# Revit family: QF_ALPENINOX_713294_AC6R4RL
name_source: partatom
category: Attrezzature speciali
revit_build: Autodesk Revit 2018 (Build: 20181011_1500(x64)
units: mm (PartAtom-declared; Revit-internal decimal feet)

## family parameters
Basato su piano di lavoro = No
Condiviso = No
Punto di calcolo locali = No
Quota connettore circolare = Usa diametro
Sempre verticale = Sì
Taglio con vuoti quando caricato = No
Tipo di parte = Normale

## types (1)
- Standard
    Accessory = Sì
    Cold Water Size = 0 mm
    Compressed Air Pressure = 0.0 Pa
    Compressed Air Size = 0 mm
    Compressed Air Volume = 0.0 L/s
    Condensate Return Size = 0 mm
    Cycle = 50 Hz
    Depth Actual = 700 mm  [stored 2.29659 ft]
    Descrizione = REFR.COUNTER 590L 2xDOOR 4x1/2DRW NOTOP REM CU_LFT A304
    Direct Waste Size = 0 mm
    Gas Input Pressure = 0
    Gas KW = 0
    Gas Size = 0 mm
    HP = 0 HP
    Height Actual = 800 mm  [stored 2.62467 ft]
    Hot Water Size = 0 mm
    Item Number = 713294
    Length Actual = 2012 mm  [stored 6.60105 ft]
    Modello = AC6R4RL
    Phase = 1
    Produttore = Alpeninox
    Refrigerant Compressor Remote = Sì
    Refrigeration Liquid Line Size = 8 mm  [stored 0.0262467 ft]
    Refrigeration Suction Line Size = 10 mm  [stored 0.0328084 ft]
    Steam Consumption per Hour = 0
    Steam Supply Maximum Pressure = 0.0 Pa
    Steam Supply Minimum Pressure = 0.0 Pa
    Steam Supply Size = 0 mm
    URL = http://www.alpeninox.com
    URL Manufacturer = http://www.alpeninox.com
    Volts = 220 V
    Watts = 30 W
    Weight = 120.00 kg

note: source unit labels omitted for Gas Input Pressure — the stored unit's dimension contradicts the parameter name (converter mislabeling)

note: [stored X ft] marks values corroborated as IEEE doubles in the binary element streams (Revit-internal decimal feet)

## geometry (parser evidence)
native form markers: Blend x28, Sweep x1
no freeform markers — native parametric forms only
